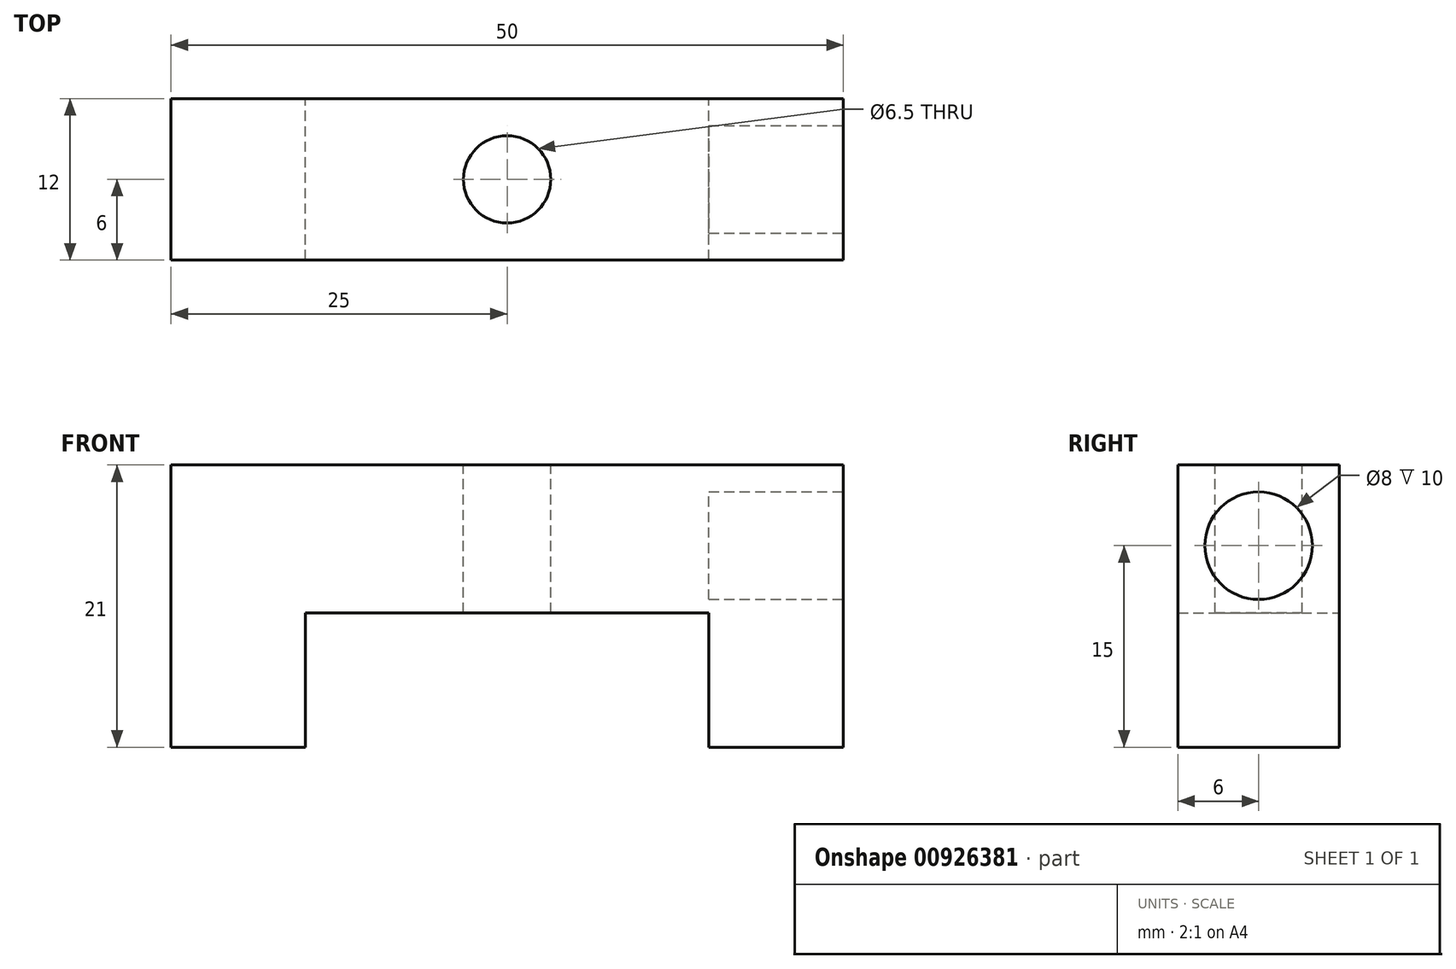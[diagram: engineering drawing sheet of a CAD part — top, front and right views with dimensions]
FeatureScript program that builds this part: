
annotation { "Feature Type Name" : "Feature", "Feature Type Description" : "" }
export const myFeature = defineFeature(function(context is Context, id is Id, definition is map)
    precondition{}
    {
        {
            var Q0;
            Q0=qCreatedBy(makeId("Front.planeOp"),FACE);
            var sketch = newSketch(context, id + "F0", { "sketchPlane" : qUnion([Q0])});
            skLineSegment(sketch, "E0", {"start": v(0, 0) * mm, "end": v(15, 0) * mm});
            skLineSegment(sketch, "E1", {"start": v(15, 0) * mm, "end": v(15, -10) * mm});
            skLineSegment(sketch, "E2", {"start": v(15, -10) * mm, "end": v(25, -10) * mm});
            skLineSegment(sketch, "E3", {"start": v(25, -10) * mm, "end": v(25, 11) * mm});
            skLineSegment(sketch, "E4", {"start": v(25, 11) * mm, "end": v(0, 11) * mm});
            skLineSegment(sketch, "E5", {"start": v(0, 11) * mm, "end": v(0, 0) * mm, "construction": true});
            skLineSegment(sketch, "E6.MirrorCS", {"start": v(-15, 0) * mm, "end": v(-15, -10) * mm});
            skLineSegment(sketch, "E7.MirrorCS", {"start": v(-25, 11) * mm, "end": v(0, 11) * mm});
            skLineSegment(sketch, "E8.MirrorCS", {"start": v(-25, -10) * mm, "end": v(-25, 11) * mm});
            skLineSegment(sketch, "E9.MirrorCS", {"start": v(-15, -10) * mm, "end": v(-25, -10) * mm});
            skLineSegment(sketch, "E10.MirrorCS", {"start": v(0, 0) * mm, "end": v(-15, 0) * mm});
            skSolve(sketch);
        }
        {
            var Q0;
            Q0 = qSketchRegion(id + "F0", true);
            extrude(context, id + "F1", {"entities" : qUnion([Q0]), "depth" : 12 * mm, "offsetDistance" : 25 * mm});
        }
        {
            var Q0;
            Q0=makeQuery(id+"F1.opExtrude","SWEPT_FACE",FACE,{"disambiguationData":[OSD([sQuery(id+"F0.wireOp",EDGE,"E3")])]});
            var sketch = newSketch(context, id + "F2", { "sketchPlane" : qUnion([Q0])});
            skCircle(sketch, "E11", {"center": v(-6, 5) * mm, "radius": 4 * mm});
            skPoint(sketch, "E11.centerSnap0", {"position": v(-6, 11) * mm});
            skSolve(sketch);
        }
        {
            var Q0;
            Q0 = qSketchRegion(id + "F2", true);
            extrude(context, id + "F3", {"entities" : qUnion([Q0]), "operationType" : NewBodyOperationType.REMOVE, "oppositeDirection" : true, "depth" : 10 * mm, "offsetDistance" : 25 * mm});
        }
        {
            var Q0;
            Q0=makeQuery(id+"F1.opExtrude","SWEPT_FACE",FACE,{"disambiguationData":[OSD([sQuery(id+"F0.wireOp",EDGE,"E4"),sQuery(id+"F0.wireOp",EDGE,"E7.MirrorCS")])]});
            var sketch = newSketch(context, id + "F4", { "sketchPlane" : qUnion([Q0])});
            skCircle(sketch, "E12", {"center": v(0, -6) * mm, "radius": 3.25 * mm});
            skSolve(sketch);
        }
        {
            var Q0;
            Q0 = qSketchRegion(id + "F4", true);
            extrude(context, id + "F5", {"entities" : qUnion([Q0]), "operationType" : NewBodyOperationType.REMOVE, "endBound" : BoundingType.THROUGH_ALL, "oppositeDirection" : true, "depth" : 25 * mm, "offsetDistance" : 25 * mm});
        }
    });
